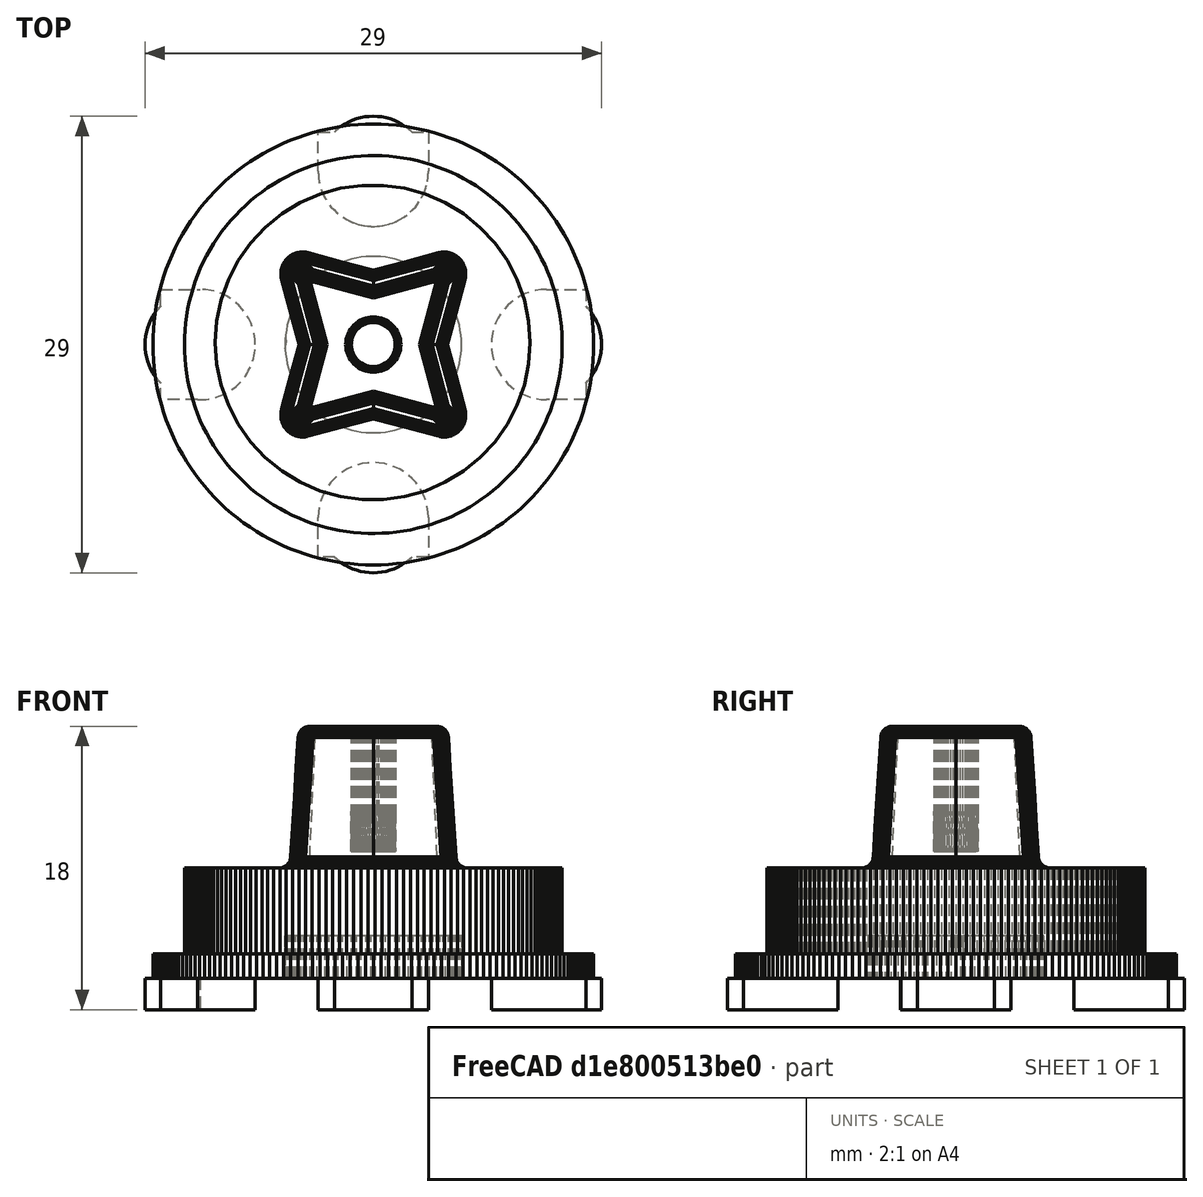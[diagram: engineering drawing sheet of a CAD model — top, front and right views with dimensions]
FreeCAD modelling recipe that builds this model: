
FCSTD DOCUMENT  (FreeCAD 0.20R29177 (Git))
Label: MotorConnect1
License: All rights reserved
LicenseURL: http://en.wikipedia.org/wiki/All_rights_reserved
objects: Sketcher::SketchObject×3, Part::Extrusion×3, Part::Fuse×3, Part::Feature×2, Mesh::Feature×1, Spreadsheet::Sheet×1, Part::Refine×1, PartDesign::Body×1
note: 13 computed .brp shape members not serialized (recipe doc carries the construction recipe); baked Part::Feature solids carry a one-line shape summary decoded from their .brp

FEATURE [Mesh::Feature] MotorConnect1
FEATURE [Spreadsheet::Sheet] Spreadsheet  label="data"
  cells = A1=coreCircleD; B1(coreCircleD)=11; A2=motorBackHoleToCenter; B2(motorBackHoleToCenter)=11; A3=motorBackHoleR; B3(motorBackHoleR)=3.5; A4=motorBackHoleRectLen; B4(motorBackHoleRectLen)=2.5; A5=bottomHeight; B5(bottomHeight)=2
FEATURE [Sketcher::SketchObject] Sketch  label="SketchMHol"
  FullyConstrained = false
  MapMode = 5
  Support = -> [XY_Plane]
  expr: Constraints[0] = Spreadsheet.motorBackHoleToCenter
  expr: Constraints[1] = Spreadsheet.motorBackHoleR * 2
  expr: Constraints[2] = Spreadsheet.motorBackHoleToCenter
  expr: Constraints[4] = Spreadsheet.motorBackHoleToCenter
  expr: Constraints[5] = Spreadsheet.motorBackHoleR * 2
  expr: Constraints[7] = Spreadsheet.motorBackHoleToCenter
  expr: Constraints[8] = Spreadsheet.motorBackHoleR * 2
  expr: Constraints[9] = Spreadsheet.motorBackHoleR * 2
  sketch-geometry (4):
    g0: Circle CenterX=-11 CenterY=-0.00404906 CenterZ=0 NormalX=0 NormalY=0 NormalZ=1 AngleXU=0 Radius=3.5
    g1: Circle CenterX=11 CenterY=0 CenterZ=0 NormalX=0 NormalY=0 NormalZ=1 AngleXU=0 Radius=3.5
    g2: Circle CenterX=0 CenterY=11 CenterZ=0 NormalX=0 NormalY=0 NormalZ=1 AngleXU=0 Radius=3.5
    g3: Circle CenterX=0 CenterY=-11 CenterZ=0 NormalX=0 NormalY=0 NormalZ=1 AngleXU=0 Radius=3.5
  constraints (10):
    c: DistanceX(g0,g-1) = 11
    c: Diameter(g0) = 7
    c: DistanceX(g-1,g1) = 11
    c: PointOnObject(g2,g-2)
    c: DistanceY(g-1,g2) = 11
    c: Diameter(g2) = 7
    c: PointOnObject(g3,g-2)
    c: DistanceY(g3,g-1) = 11
    c: Diameter(g3) = 7
    c: Diameter(g1) = 7
FEATURE [Sketcher::SketchObject] Sketch001  label="SketchRects"
  FullyConstrained = true
  MapMode = 2
  Support = -> [Sketch]
  expr: Constraints[34] = Spreadsheet.motorBackHoleR
  expr: Constraints[35] = Spreadsheet.motorBackHoleR
  expr: Constraints[36] = Spreadsheet.motorBackHoleR
  expr: Constraints[37] = Spreadsheet.motorBackHoleR
  expr: Constraints[38] = Spreadsheet.motorBackHoleR
  expr: Constraints[39] = Spreadsheet.motorBackHoleR
  expr: Constraints[40] = Spreadsheet.motorBackHoleRectLen
  expr: Constraints[41] = Spreadsheet.motorBackHoleRectLen
  expr: Constraints[42] = Spreadsheet.motorBackHoleRectLen
  expr: Constraints[43] = Spreadsheet.motorBackHoleRectLen
  expr: Constraints[44] = Spreadsheet.motorBackHoleToCenter
  expr: Constraints[45] = Spreadsheet.motorBackHoleToCenter
  expr: Constraints[46] = Spreadsheet.motorBackHoleToCenter
  expr: Constraints[47] = Spreadsheet.motorBackHoleToCenter
  expr: Constraints[8] = Spreadsheet.motorBackHoleR
  expr: Constraints[9] = Spreadsheet.motorBackHoleR
  sketch-geometry (16):
    g0: LineSegment StartX=-13.5 StartY=3.5 StartZ=0 EndX=-11 EndY=3.5 EndZ=0
    g1: LineSegment StartX=-11 StartY=3.5 StartZ=0 EndX=-11 EndY=-3.5 EndZ=0
    g2: LineSegment StartX=-11 StartY=-3.5 StartZ=0 EndX=-13.5 EndY=-3.5 EndZ=0
    g3: LineSegment StartX=-13.5 StartY=-3.5 StartZ=0 EndX=-13.5 EndY=3.5 EndZ=0
    g4: LineSegment StartX=-3.5 StartY=13.5 StartZ=0 EndX=3.5 EndY=13.5 EndZ=0
    g5: LineSegment StartX=3.5 StartY=13.5 StartZ=0 EndX=3.5 EndY=11 EndZ=0
    g6: LineSegment StartX=3.5 StartY=11 StartZ=0 EndX=-3.5 EndY=11 EndZ=0
    g7: LineSegment StartX=-3.5 StartY=11 StartZ=0 EndX=-3.5 EndY=13.5 EndZ=0
    g8: LineSegment StartX=11 StartY=3.5 StartZ=0 EndX=13.5 EndY=3.5 EndZ=0
    g9: LineSegment StartX=13.5 StartY=3.5 StartZ=0 EndX=13.5 EndY=-3.5 EndZ=0
    g10: LineSegment StartX=13.5 StartY=-3.5 StartZ=0 EndX=11 EndY=-3.5 EndZ=0
    g11: LineSegment StartX=11 StartY=-3.5 StartZ=0 EndX=11 EndY=3.5 EndZ=0
    g12: LineSegment StartX=-3.5 StartY=-11 StartZ=0 EndX=3.5 EndY=-11 EndZ=0
    g13: LineSegment StartX=3.5 StartY=-11 StartZ=0 EndX=3.5 EndY=-13.5 EndZ=0
    g14: LineSegment StartX=3.5 StartY=-13.5 StartZ=0 EndX=-3.5 EndY=-13.5 EndZ=0
    g15: LineSegment StartX=-3.5 StartY=-13.5 StartZ=0 EndX=-3.5 EndY=-11 EndZ=0
  constraints (48):
    c: Coincident(g0,g1)
    c: Coincident(g1,g2)
    c: Coincident(g2,g3)
    c: Coincident(g3,g0)
    c: Horizontal(g0)
    c: Horizontal(g2)
    c: Vertical(g1)
    c: Vertical(g3)
    c: DistanceY(g-1,g0) = 3.5
    c: DistanceY(g1,g-1) = 3.5
    c: Coincident(g4,g5)
    c: Coincident(g5,g6)
    c: Coincident(g6,g7)
    c: Coincident(g7,g4)
    c: Horizontal(g4)
    c: Horizontal(g6)
    c: Vertical(g5)
    c: Vertical(g7)
    c: Coincident(g8,g9)
    c: Coincident(g9,g10)
    c: Coincident(g10,g11)
    c: Coincident(g11,g8)
    c: Horizontal(g8)
    c: Horizontal(g10)
    c: Vertical(g9)
    c: Vertical(g11)
    c: Coincident(g12,g13)
    c: Coincident(g13,g14)
    c: Coincident(g14,g15)
    c: Coincident(g15,g12)
    c: Horizontal(g12)
    c: Horizontal(g14)
    c: Vertical(g13)
    c: Vertical(g15)
    c: DistanceX(g6,g-1) = 3.5
    c: DistanceX(g-1,g5) = 3.5
    c: DistanceX(g12,g-1) = 3.5
    c: DistanceX(g-1,g12) = 3.5
    c: DistanceY(g-1,g8) = 3.5
    c: DistanceY(g10,g-1) = 3.5
    c: DistanceX(g0,g0) = 2.5
    c: DistanceX(g8,g8) = 2.5
    c: DistanceY(g5,g4) = 2.5
    c: DistanceY(g13,g12) = 2.5
    c: DistanceX(g0,g-1) = 11
    c: DistanceX(g-1,g8) = 11
    c: DistanceY(g-1,g5) = 11
    c: DistanceY(g12,g-1) = 11
FEATURE [Part::Extrusion] Extrude  label="ExtrudeBottomHole"
  Base = -> Sketch
  Dir = (0,0,1)
  DirMode = 2
  FaceMakerClass = Part::FaceMakerBullseye
  LengthFwd = -2
  LengthRev = 0
  Solid = true
  Symmetric = false
  expr: LengthFwd = -Spreadsheet.bottomHeight
FEATURE [Part::Extrusion] Extrude001  label="ExtrudeBottomRect"
  Base = -> Sketch001
  Dir = (0,0,1)
  DirMode = 2
  FaceMakerClass = Part::FaceMakerBullseye
  LengthFwd = -2
  LengthRev = 0
  Solid = true
  Symmetric = false
  expr: LengthFwd = -Spreadsheet.bottomHeight
FEATURE [Part::Fuse] Fusion  label="FusionBottom"
  Base = -> Extrude
  Tool = -> Extrude001
FEATURE [Part::Feature] MotorConnect1001
  shape: bbox 28 x 28 x 16 mm, 9394 faces, 0 solids (baked)
FEATURE [Part::Feature] MotorConnect1001_solid  label="MotorConnect1001 (Solid)"
  shape: bbox 28 x 28 x 16 mm, 9394 faces (baked)
FEATURE [Part::Refine] MotorConnect1001_solid001  label="MotorConnect1001 (Solid)001"
  Source = -> MotorConnect1001_solid
FEATURE [Part::Fuse] Fusion001  label="FusionResult"
  Base = -> Fusion
  Tool = -> MotorConnect1001_solid001
FEATURE [Sketcher::SketchObject] Sketch002
  FullyConstrained = false
  MapMode = 5
  Support = -> [XY_Plane]
  sketch-geometry (1):
    g0: Circle CenterX=0 CenterY=7.45568 CenterZ=0 NormalX=0 NormalY=0 NormalZ=1 AngleXU=0 Radius=1.55095
  constraints (1):
    c: PointOnObject(g0,g-2)
FEATURE [PartDesign::Body] Body
  Group = -> [Sketch,Sketch001,Sketch002]
  Origin = -> Origin
FEATURE [Part::Extrusion] Extrude003  label="ExtrudeMissedHole"
  Base = -> Sketch002
  Dir = (0,0,1)
  DirMode = 2
  FaceMakerClass = Part::FaceMakerBullseye
  LengthFwd = 4
  LengthRev = 0
  Solid = true
  Symmetric = false
FEATURE [Part::Fuse] Fusion002  label="FusionTotalResult"
  Base = -> Fusion001
  Tool = -> Extrude003
